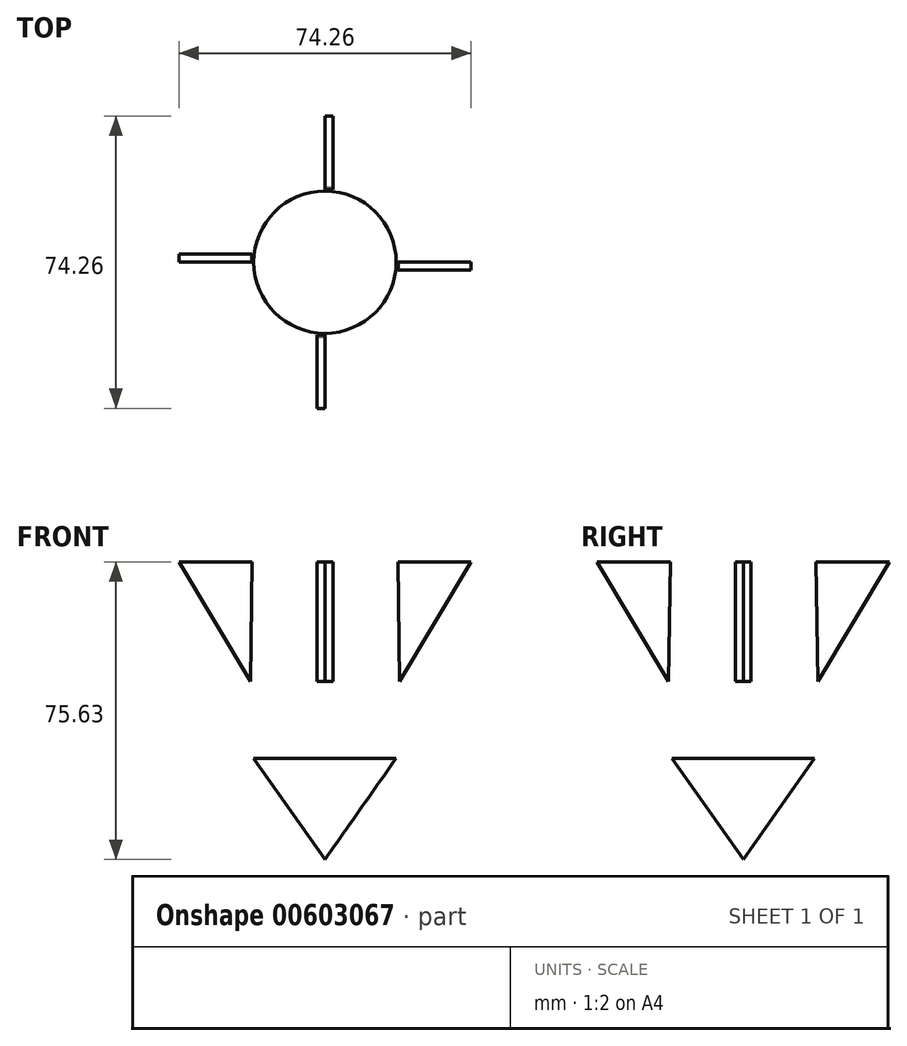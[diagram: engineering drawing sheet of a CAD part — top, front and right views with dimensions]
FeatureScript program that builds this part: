
annotation { "Feature Type Name" : "Feature", "Feature Type Description" : "" }
export const myFeature = defineFeature(function(context is Context, id is Id, definition is map)
    precondition{}
    {
        {
            var Q0;
            Q0=qCreatedBy(makeId("Top.planeOp"),FACE);
            var sketch = newSketch(context, id + "F0", { "sketchPlane" : qUnion([Q0])});
            skCircle(sketch, "E0", {"center": v(0, 0) * mm, "radius": 18.7 * mm});
            skSolve(sketch);
        }
        {
            var Q0;
            Q0=sQuery(id+"F0.wireOp",EDGE,"E0");
            extrude(context, id + "F1", {"bodyType" : ToolBodyType.SURFACE, "surfaceEntities" : qUnion([Q0]), "depth" : 50 * mm, "offsetDistance" : 25 * mm});
        }
        {
            var Q0;
            Q0=qCreatedBy(makeId("Front.planeOp"),FACE);
            var sketch = newSketch(context, id + "F2", { "sketchPlane" : qUnion([Q0])});
            skLineSegment(sketch, "E1", {"start": v(0, 0) * mm, "end": v(0, -25.74) * mm});
            skLineSegment(sketch, "E2", {"start": v(0, -25.74) * mm, "end": v(18.1, 0) * mm});
            skLineSegment(sketch, "E3", {"start": v(18.1, 0) * mm, "end": v(0, 0) * mm});
            skSolve(sketch);
        }
        {
            var Q0;
            Q0=makeQuery(id+"F2.imprint","IMPRINT",FACE,{"disambiguationData":[TD([[makeQuery(id+"F2.imprint","IMPRINT",EDGE,{"derivedFrom":sQuery(id+"F2.wireOp",EDGE,"E1")}),1.0]])]});
            var Q1;
            Q1=sQuery(id+"F2.wireOp",EDGE,"E1");
            revolve(context, id + "F3", {"entities" : qUnion([Q0]), "axis" : qUnion([Q1]), "revolveType" : RevolveType.FULL});
        }
        {
            var Q0;
            Q0=qCreatedBy(makeId("Right.planeOp"),FACE);
            var sketch = newSketch(context, id + "F4", { "sketchPlane" : qUnion([Q0])});
            skLineSegment(sketch, "E4", {"start": v(18.97, 19.54) * mm, "end": v(37.13, 49.9) * mm});
            skLineSegment(sketch, "E5", {"start": v(37.13, 49.9) * mm, "end": v(18.5, 49.9) * mm});
            skLineSegment(sketch, "E6", {"start": v(18.5, 49.9) * mm, "end": v(18.97, 19.54) * mm});
            skSolve(sketch);
        }
        {
            var Q0;
            Q0=makeQuery(id+"F4.imprint","IMPRINT",FACE,{"disambiguationData":[TD([[makeQuery(id+"F4.imprint","IMPRINT",EDGE,{"derivedFrom":sQuery(id+"F4.wireOp",EDGE,"E4")}),1.0]])]});
            extrude(context, id + "F5", {"entities" : qUnion([Q0]), "depth" : 2 * mm, "offsetDistance" : 25 * mm});
        }
        {
            var Q0;
            Q0=qCreatedBy(makeId("Right.planeOp"),FACE);
            var sketch = newSketch(context, id + "F6", { "sketchPlane" : qUnion([Q0])});
            skLineSegment(sketch, "E7", {"start": v(0, 0) * mm, "end": v(0, 49.43) * mm});
            skSolve(sketch);
        }
        {
            var Q0;
            Q0=makeQuery(id+"F5.opExtrude","SWEPT_BODY",BODY,{"disambiguationData":[OSD([sQuery(id+"F4.wireOp",EDGE,"E4"),sQuery(id+"F4.wireOp",EDGE,"E5"),sQuery(id+"F4.wireOp",EDGE,"E6")])]});
            var Q1;
            Q1=sQuery(id+"F6.wireOp",EDGE,"E7");
            circularPattern(context, id + "F7", {"entities" : qUnion([Q0]), "axis" : qUnion([Q1]), "angle" : 360 * degree, "instanceCount" : 4, "equalSpace" : true});
        }
    });
